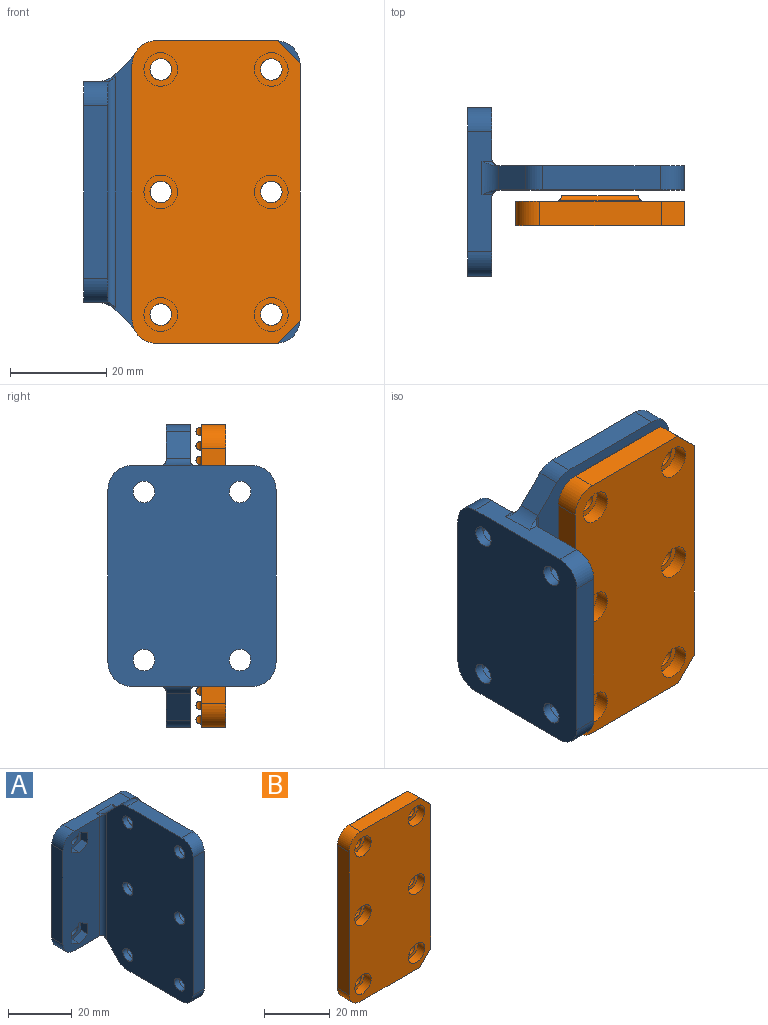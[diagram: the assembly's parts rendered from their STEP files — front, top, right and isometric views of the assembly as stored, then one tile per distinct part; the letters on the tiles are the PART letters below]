
ASSEMBLY  parts=2 mates=1
PART A: 118 faces, bbox 35x45x63 mm
  f0: cylinder r=2.25mm len=4.5mm, axis (-1,0,0), area 28.3mm2, adj f7,f87
  f1: cylinder r=2.25mm len=4.5mm, axis (-1,0,0), area 28.3mm2, adj f7,f80
  f2: cylinder r=2.25mm len=4.5mm, axis (-1,0,0), area 28.3mm2, adj f7,f73
  f3: cylinder r=2.25mm len=4.5mm, axis (-1,0,0), area 28.3mm2, adj f7,f66
  f4: cylinder r=2.25mm len=4.5mm, axis (-1,0,0), area 28.3mm2, adj f7,f59
  f5: cylinder r=2.25mm len=4.5mm, axis (-1,0,0), area 28.3mm2, adj f7,f52
  f6: plane 24.43x5mm, normal (0,0,1), area 122.1mm2, adj f7,f8,f95,f98
  f7: plane 63x39.07mm, normal (-1,0,0), area 2269.5mm2, adj f0,f1,f2,f3,f4,f5,f6,f20
  f8: plane 63x39.07mm, normal (1,0,0), area 2110.8mm2, adj f6,f20,f21,f50,f51,f53,f54,f55
  f9: cylinder r=2.25mm len=4.5mm, axis (0,1,0), area 28.3mm2, adj f19,f35
  f10: cylinder r=2.25mm len=4.5mm, axis (0,1,0), area 28.3mm2, adj f19,f28
  f11: cylinder r=2.25mm len=4.5mm, axis (0,1,0), area 28.3mm2, adj f19,f49
  f12: cylinder r=2.25mm len=4.5mm, axis (0,1,0), area 28.3mm2, adj f19,f42
  f13: plane 46x16.4mm, normal (0,-1,0), area 658.8mm2, adj f16,f17,f18,f22,f23,f24,f25,f26
  f14: plane 46x10.6mm, normal (0,-1,0), area 395.4mm2, adj f15,f16,f18,f36,f37,f38,f39,f41
  f15: plane 36x5mm, normal (1,0,0), area 180mm2, adj f14,f19,f100,f103
  f16: plane 25x5.09mm, normal (0,0,1), area 110.5mm2, adj f13,f14,f19,f97,f100,f101,f112,f113
  f17: plane 36x5mm, normal (-1,0,0), area 180mm2, adj f13,f19,f101,f102
  f18: plane 25x5.09mm, normal (0,0,-1), area 110.5mm2, adj f13,f14,f19,f96,f102,f103,f104,f113
  f19: plane 46x35mm, normal (0,1,0), area 1524.9mm2, adj f9,f10,f11,f12,f15,f16,f17,f18
  f20: plane 24.43x5mm, normal (0,0,-1), area 122.1mm2, adj f7,f8,f94,f99
  f21: plane 53x5mm, normal (0,-1,0), area 265mm2, adj f7,f8,f98,f99
  f22: plane 3.5x3mm, normal (0.5,0,0.87), area 12.1mm2, adj f13,f23,f27,f28
  f23: plane 3.5x3mm, normal (-0.5,0,0.87), area 12.1mm2, adj f13,f22,f24,f28
  f24: plane 4.04x3mm, normal (-1,0,0), area 12.1mm2, adj f13,f23,f25,f28
  f25: plane 3.5x3mm, normal (-0.5,0,-0.87), area 12.1mm2, adj f13,f24,f26,f28
  f26: plane 3.5x3mm, normal (0.5,0,-0.87), area 12.1mm2, adj f13,f25,f27,f28
  f27: plane 4.04x3mm, normal (1,0,0), area 12.1mm2, adj f13,f22,f26,f28
  f28: plane 8.08x7mm, normal (0,-1,0), area 26.5mm2, adj f10,f22,f23,f24,f25,f26,f27
  f29: plane 3.5x3mm, normal (0.5,0,0.87), area 12.1mm2, adj f13,f30,f34,f35
  f30: plane 3.5x3mm, normal (-0.5,0,0.87), area 12.1mm2, adj f13,f29,f31,f35
  f31: plane 4.04x3mm, normal (-1,0,0), area 12.1mm2, adj f13,f30,f32,f35
  f32: plane 3.5x3mm, normal (-0.5,0,-0.87), area 12.1mm2, adj f13,f31,f33,f35
  f33: plane 3.5x3mm, normal (0.5,0,-0.87), area 12.1mm2, adj f13,f32,f34,f35
  f34: plane 4.04x3mm, normal (1,0,0), area 12.1mm2, adj f13,f29,f33,f35
  f35: plane 8.08x7mm, normal (0,-1,0), area 26.5mm2, adj f9,f29,f30,f31,f32,f33,f34
  f36: plane 3.5x3mm, normal (-0.5,0,0.87), area 12.1mm2, adj f14,f37,f41,f42
  f37: plane 4.04x3mm, normal (-1,0,0), area 12.1mm2, adj f14,f36,f38,f42
  f38: plane 3.5x3mm, normal (-0.5,0,-0.87), area 12.1mm2, adj f14,f37,f39,f42
  f39: plane 3.51x3.01mm, normal (0.5,0,-0.87), area 12.1mm2, adj f14,f38,f40,f42,f107
  f40: plane 4.04x3mm, normal (1,0,0), area 12.1mm2, adj f39,f41,f42,f106
  f41: plane 3.5x3mm, normal (0.5,0,0.87), area 12.1mm2, adj f14,f36,f40,f42,f105
  f42: plane 8.08x7mm, normal (0,-1,0), area 26.5mm2, adj f12,f36,f37,f38,f39,f40,f41
  f43: plane 3.5x3mm, normal (-0.5,0,0.87), area 12.1mm2, adj f14,f44,f48,f49
  f44: plane 4.04x3mm, normal (-1,0,0), area 12.1mm2, adj f14,f43,f45,f49
  f45: plane 3.5x3mm, normal (-0.5,0,-0.87), area 12.1mm2, adj f14,f44,f46,f49
  f46: plane 3.51x3.01mm, normal (0.5,0,-0.87), area 12.1mm2, adj f14,f45,f47,f49,f111
  f47: plane 4.04x3mm, normal (1,0,0), area 12.1mm2, adj f46,f48,f49,f110
  f48: plane 3.5x3mm, normal (0.5,0,0.87), area 12.1mm2, adj f14,f43,f47,f49,f109
  f49: plane 8.08x7mm, normal (0,-1,0), area 26.5mm2, adj f11,f43,f44,f45,f46,f47,f48
  f50: plane 5.57x5.57mm, normal (0,0.71,0.71), area 39.4mm2, adj f7,f8,f95,f97
  f51: plane 5.57x5.57mm, normal (0,0.71,-0.71), area 39.4mm2, adj f7,f8,f94,f96
  f52: plane 8.08x7mm, normal (1,0,0), area 26.5mm2, adj f5,f53,f54,f55,f56,f57,f58
  f53: plane 3.5x3mm, normal (0,0.5,-0.87), area 12.1mm2, adj f8,f52,f54,f58
  f54: plane 4.04x3mm, normal (0,1,0), area 12.1mm2, adj f8,f52,f53,f55
  f55: plane 3.5x3mm, normal (0,0.5,0.87), area 12.1mm2, adj f8,f52,f54,f56
  f56: plane 3.5x3mm, normal (0,-0.5,0.87), area 12.1mm2, adj f8,f52,f55,f57
  f57: plane 4.04x3mm, normal (0,-1,0), area 12.1mm2, adj f8,f52,f56,f58
  f58: plane 3.5x3mm, normal (0,-0.5,-0.87), area 12.1mm2, adj f8,f52,f53,f57
  f59: plane 8.08x7mm, normal (1,0,0), area 26.5mm2, adj f4,f60,f61,f62,f63,f64,f65
  f60: plane 3.5x3mm, normal (0,0.5,-0.87), area 12.1mm2, adj f8,f59,f61,f65
  f61: plane 4.04x3mm, normal (0,1,0), area 12.1mm2, adj f8,f59,f60,f62
  f62: plane 3.5x3mm, normal (0,0.5,0.87), area 12.1mm2, adj f8,f59,f61,f63
  f63: plane 3.5x3mm, normal (0,-0.5,0.87), area 12.1mm2, adj f8,f59,f62,f64
  f64: plane 4.04x3mm, normal (0,-1,0), area 12.1mm2, adj f8,f59,f63,f65
  f65: plane 3.5x3mm, normal (0,-0.5,-0.87), area 12.1mm2, adj f8,f59,f60,f64
  f66: plane 8.08x7mm, normal (1,0,0), area 26.5mm2, adj f3,f67,f68,f69,f70,f71,f72
  f67: plane 3.5x3mm, normal (0,0.5,-0.87), area 12.1mm2, adj f8,f66,f68,f72
  f68: plane 4.04x3mm, normal (0,1,0), area 12.1mm2, adj f8,f66,f67,f69
  f69: plane 3.5x3mm, normal (0,0.5,0.87), area 12.1mm2, adj f8,f66,f68,f70
  f70: plane 3.5x3mm, normal (0,-0.5,0.87), area 12.1mm2, adj f8,f66,f69,f71
  f71: plane 4.04x3mm, normal (0,-1,0), area 12.1mm2, adj f8,f66,f70,f72
  f72: plane 3.5x3mm, normal (0,-0.5,-0.87), area 12.1mm2, adj f8,f66,f67,f71
  f73: plane 8.08x7mm, normal (1,0,0), area 26.5mm2, adj f2,f74,f75,f76,f77,f78,f79
  f74: plane 3.5x3mm, normal (0,-0.5,0.87), area 12.1mm2, adj f8,f73,f75,f79
  f75: plane 4.04x3mm, normal (0,-1,0), area 12.1mm2, adj f8,f73,f74,f76
  f76: plane 3.5x3mm, normal (0,-0.5,-0.87), area 12.1mm2, adj f8,f73,f75,f77
  f77: plane 3.5x3mm, normal (0,0.5,-0.87), area 12.1mm2, adj f8,f73,f76,f78
  f78: plane 4.04x3mm, normal (0,1,0), area 12.1mm2, adj f8,f73,f77,f79
  f79: plane 3.5x3mm, normal (0,0.5,0.87), area 12.1mm2, adj f8,f73,f74,f78
  f80: plane 8.08x7mm, normal (1,0,0), area 26.5mm2, adj f1,f81,f82,f83,f84,f85,f86
  f81: plane 3.5x3mm, normal (0,-0.5,0.87), area 12.1mm2, adj f8,f80,f82,f86
  f82: plane 4.04x3mm, normal (0,-1,0), area 12.1mm2, adj f8,f80,f81,f83
  f83: plane 3.5x3mm, normal (0,-0.5,-0.87), area 12.1mm2, adj f8,f80,f82,f84
  f84: plane 3.5x3mm, normal (0,0.5,-0.87), area 12.1mm2, adj f8,f80,f83,f85
  f85: plane 4.04x3mm, normal (0,1,0), area 12.1mm2, adj f8,f80,f84,f86
  f86: plane 3.5x3mm, normal (0,0.5,0.87), area 12.1mm2, adj f8,f80,f81,f85
  f87: plane 8.08x7mm, normal (1,0,0), area 26.5mm2, adj f0,f88,f89,f90,f91,f92,f93
  f88: plane 3.5x3mm, normal (0,-0.5,0.87), area 12.1mm2, adj f8,f87,f89,f93
  f89: plane 4.04x3mm, normal (0,-1,0), area 12.1mm2, adj f8,f87,f88,f90
  f90: plane 3.5x3mm, normal (0,-0.5,-0.87), area 12.1mm2, adj f8,f87,f89,f91
  f91: plane 3.5x3mm, normal (0,0.5,-0.87), area 12.1mm2, adj f8,f87,f90,f92
  f92: plane 4.04x3mm, normal (0,1,0), area 12.1mm2, adj f8,f87,f91,f93
  f93: plane 3.5x3mm, normal (0,0.5,0.87), area 12.1mm2, adj f8,f87,f88,f92
  f94: cylinder r=5mm len=5mm, axis (1,0,0), area 19.6mm2, adj f7,f8,f20,f51
  f95: cylinder r=5mm len=5mm, axis (1,0,0), area 19.6mm2, adj f6,f7,f8,f50
  f96: cylinder r=5mm len=7mm, axis (-1,0,0), area 22.9mm2, adj f7,f8,f18,f51,f116,f117
  f97: cylinder r=5mm len=7mm, axis (1,0,0), area 22.9mm2, adj f7,f8,f16,f50,f114,f115
  f98: cylinder r=5mm len=5mm, axis (1,0,0), area 39.3mm2, adj f6,f7,f8,f21
  f99: cylinder r=5mm len=5mm, axis (-1,0,0), area 39.3mm2, adj f7,f8,f20,f21
  f100: cylinder r=5mm len=5mm, axis (0,-1,0), area 39.3mm2, adj f14,f15,f16,f19
  f101: cylinder r=5mm len=5mm, axis (0,1,0), area 39.3mm2, adj f13,f16,f17,f19
  f102: cylinder r=5mm len=5mm, axis (0,-1,0), area 39.3mm2, adj f13,f17,f18,f19
  f103: cylinder r=5mm len=5mm, axis (0,1,0), area 39.3mm2, adj f14,f15,f18,f19
  f104: cylinder r=1.5mm len=4.25mm, axis (0,0,1), area 8.6mm2, adj f8,f14,f18,f105,f117
  f105: bspline ~1.54x1.54mm, area 0.8mm2, adj f8,f41,f104,f106
  f106: cylinder r=1.5mm len=4.04mm, axis (0,0,-1), area 7.4mm2, adj f8,f40,f105,f107
  f107: bspline ~1.54x1.53mm, area 0.8mm2, adj f8,f39,f106,f108
  f108: cylinder r=1.5mm len=30.5mm, axis (0,0,1), area 71.9mm2, adj f8,f14,f107,f109
  f109: bspline ~1.54x1.54mm, area 0.8mm2, adj f8,f48,f108,f110
  f110: cylinder r=1.5mm len=4.04mm, axis (0,0,-1), area 7.4mm2, adj f8,f47,f109,f111
  f111: bspline ~1.54x1.53mm, area 0.8mm2, adj f8,f46,f110,f112
  f112: cylinder r=1.5mm len=4.25mm, axis (0,0,1), area 8.6mm2, adj f8,f14,f16,f111,f115
  f113: cylinder r=1.5mm len=48mm, axis (0,0,-1), area 110.2mm2, adj f7,f13,f16,f18,f114,f116
  f114: cylinder r=1mm len=3.57mm, axis (0,-1,0), area 2.1mm2, adj f7,f16,f97,f113
  f115: cylinder r=1mm len=3.57mm, axis (0,-1,0), area 2.1mm2, adj f8,f16,f97,f112
  f116: cylinder r=1mm len=3.57mm, axis (0,-1,0), area 2.1mm2, adj f7,f18,f96,f113
  f117: cylinder r=1mm len=3.57mm, axis (0,-1,0), area 2.1mm2, adj f8,f18,f96,f104
PART B: 175 faces, bbox 35x6.2x63 mm
  f0: plane 63x35mm, normal (0,1,0), area 1206.4mm2, adj f1,f2,f3,f4,f5,f6,f7,f8
  f1: cylinder r=2.25mm len=4.5mm, axis (0,1,0), area 28.3mm2, adj f0,f17
  f2: cylinder r=2.25mm len=4.5mm, axis (0,1,0), area 28.3mm2, adj f0,f19
  f3: cylinder r=2.25mm len=4.5mm, axis (0,1,0), area 28.3mm2, adj f0,f21
  f4: cylinder r=2.25mm len=4.5mm, axis (0,1,0), area 28.3mm2, adj f0,f23
  f5: cylinder r=2.25mm len=4.5mm, axis (0,1,0), area 28.3mm2, adj f0,f13
  f6: cylinder r=2.25mm len=4.5mm, axis (0,1,0), area 28.3mm2, adj f0,f15
  f7: plane 53.4x5mm, normal (1,0,0), area 267mm2, adj f0,f11,f173,f174
  f8: plane 25.2x5mm, normal (0,0,1), area 126mm2, adj f0,f11,f171,f174
  f9: plane 53x5mm, normal (-1,0,0), area 265mm2, adj f0,f11,f171,f172
  f10: plane 25.2x5mm, normal (0,0,-1), area 126mm2, adj f0,f11,f172,f173
  f11: plane 63x35mm, normal (0,-1,0), area 1940.3mm2, adj f7,f8,f9,f10,f12,f14,f16,f18
  f12: cylinder r=3.5mm len=7mm, axis (0,-1,0), area 66mm2, adj f11,f13
  f13: plane 7x7mm, normal (0,-1,0), area 22.6mm2, adj f5,f12
  f14: cylinder r=3.5mm len=7mm, axis (0,-1,0), area 66mm2, adj f11,f15
  f15: plane 7x7mm, normal (0,-1,0), area 22.6mm2, adj f6,f14
  f16: cylinder r=3.5mm len=7mm, axis (0,-1,0), area 66mm2, adj f11,f17
  f17: plane 7x7mm, normal (0,-1,0), area 22.6mm2, adj f1,f16
  f18: cylinder r=3.5mm len=7mm, axis (0,-1,0), area 66mm2, adj f11,f19
  f19: plane 7x7mm, normal (0,-1,0), area 22.6mm2, adj f2,f18
  f20: cylinder r=3.5mm len=7mm, axis (0,-1,0), area 66mm2, adj f11,f21
  f21: plane 7x7mm, normal (0,-1,0), area 22.6mm2, adj f3,f20
  f22: cylinder r=3.5mm len=7mm, axis (0,-1,0), area 66mm2, adj f11,f23
  f23: plane 7x7mm, normal (0,-1,0), area 22.6mm2, adj f4,f22
  f24: cylinder r=0.26mm len=18.33mm, axis (-1,0,0), area 7.3mm2, adj f0,f25,f169,f170
  f25: cylinder r=0.87mm len=16.84mm, axis (-1,0,0), area 45.2mm2, adj f24,f26,f27,f28,f169,f170
  f26: cylinder r=0.26mm len=18.33mm, axis (-1,0,0), area 7.3mm2, adj f0,f25,f169,f170
  f27: plane 0.19x0.01mm, normal (1,0,0), area 0mm2, adj f25,f170
  f28: plane 0.19x0.01mm, normal (-1,0,0), area 0mm2, adj f25,f169
  f29: cylinder r=0.26mm len=18.33mm, axis (-1,0,0), area 7.3mm2, adj f0,f31,f167,f168
  f30: cylinder r=0.26mm len=18.33mm, axis (-1,0,0), area 7.3mm2, adj f0,f31,f167,f168
  f31: cylinder r=0.87mm len=16.84mm, axis (-1,0,0), area 45.2mm2, adj f29,f30,f32,f33,f167,f168
  f32: plane 0.19x0.01mm, normal (1,0,0), area 0mm2, adj f31,f168
  f33: plane 0.19x0.01mm, normal (-1,0,0), area 0mm2, adj f31,f167
  f34: cylinder r=0.26mm len=18.33mm, axis (-1,0,0), area 7.3mm2, adj f0,f36,f165,f166
  f35: cylinder r=0.26mm len=18.33mm, axis (-1,0,0), area 7.3mm2, adj f0,f36,f165,f166
  f36: cylinder r=0.87mm len=16.84mm, axis (-1,0,0), area 45.2mm2, adj f34,f35,f37,f38,f165,f166
  f37: plane 0.19x0.01mm, normal (1,0,0), area 0mm2, adj f36,f166
  f38: plane 0.19x0.01mm, normal (-1,0,0), area 0mm2, adj f36,f165
  f39: cylinder r=0.26mm len=18.33mm, axis (-1,0,0), area 7.3mm2, adj f0,f40,f163,f164
  f40: cylinder r=0.87mm len=16.84mm, axis (-1,0,0), area 45.2mm2, adj f39,f41,f42,f43,f163,f164
  f41: cylinder r=0.26mm len=18.33mm, axis (-1,0,0), area 7.3mm2, adj f0,f40,f163,f164
  f42: plane 0.19x0.01mm, normal (1,0,0), area 0mm2, adj f40,f164
  f43: plane 0.19x0.01mm, normal (-1,0,0), area 0mm2, adj f40,f163
  f44: cylinder r=0.26mm len=18.33mm, axis (-1,0,0), area 7.3mm2, adj f0,f46,f161,f162
  f45: cylinder r=0.26mm len=18.33mm, axis (-1,0,0), area 7.3mm2, adj f0,f46,f161,f162
  f46: cylinder r=0.87mm len=16.84mm, axis (-1,0,0), area 45.2mm2, adj f44,f45,f47,f48,f161,f162
  f47: plane 0.19x0.01mm, normal (1,0,0), area 0mm2, adj f46,f162
  f48: plane 0.19x0.01mm, normal (-1,0,0), area 0mm2, adj f46,f161
  f49: cylinder r=0.26mm len=18.33mm, axis (-1,0,0), area 7.3mm2, adj f0,f50,f159,f160
  f50: cylinder r=0.87mm len=16.84mm, axis (-1,0,0), area 45.2mm2, adj f49,f51,f52,f53,f159,f160
  f51: cylinder r=0.26mm len=18.33mm, axis (-1,0,0), area 7.3mm2, adj f0,f50,f159,f160
  f52: plane 0.19x0.01mm, normal (1,0,0), area 0mm2, adj f50,f160
  f53: plane 0.19x0.01mm, normal (-1,0,0), area 0mm2, adj f50,f159
  f54: cylinder r=0.26mm len=18.33mm, axis (-1,0,0), area 7.3mm2, adj f0,f56,f157,f158
  f55: cylinder r=0.26mm len=18.33mm, axis (-1,0,0), area 7.3mm2, adj f0,f56,f157,f158
  f56: cylinder r=0.87mm len=16.84mm, axis (-1,0,0), area 45.2mm2, adj f54,f55,f57,f58,f157,f158
  f57: plane 0.19x0.01mm, normal (1,0,0), area 0mm2, adj f56,f158
  f58: plane 0.19x0.01mm, normal (-1,0,0), area 0mm2, adj f56,f157
  f59: cylinder r=0.26mm len=18.33mm, axis (-1,0,0), area 7.3mm2, adj f0,f60,f155,f156
  f60: cylinder r=0.87mm len=16.84mm, axis (-1,0,0), area 45.2mm2, adj f59,f61,f62,f63,f155,f156
  f61: cylinder r=0.26mm len=18.33mm, axis (-1,0,0), area 7.3mm2, adj f0,f60,f155,f156
  f62: plane 0.19x0.01mm, normal (1,0,0), area 0mm2, adj f60,f156
  f63: plane 0.19x0.01mm, normal (-1,0,0), area 0mm2, adj f60,f155
  f64: cylinder r=0.26mm len=18.33mm, axis (-1,0,0), area 7.3mm2, adj f0,f66,f153,f154
  f65: cylinder r=0.26mm len=18.33mm, axis (-1,0,0), area 7.3mm2, adj f0,f66,f153,f154
  f66: cylinder r=0.87mm len=16.84mm, axis (-1,0,0), area 45.2mm2, adj f64,f65,f67,f68,f153,f154
  f67: plane 0.19x0.01mm, normal (1,0,0), area 0mm2, adj f66,f154
  f68: plane 0.19x0.01mm, normal (-1,0,0), area 0mm2, adj f66,f153
  f69: cylinder r=0.26mm len=18.33mm, axis (-1,0,0), area 7.3mm2, adj f0,f70,f151,f152
  f70: cylinder r=0.87mm len=16.84mm, axis (-1,0,0), area 45.2mm2, adj f69,f71,f72,f73,f151,f152
  f71: cylinder r=0.26mm len=18.33mm, axis (-1,0,0), area 7.3mm2, adj f0,f70,f151,f152
  f72: plane 0.19x0.01mm, normal (1,0,0), area 0mm2, adj f70,f152
  f73: plane 0.19x0.01mm, normal (-1,0,0), area 0mm2, adj f70,f151
  f74: cylinder r=0.26mm len=18.33mm, axis (-1,0,0), area 7.3mm2, adj f0,f76,f149,f150
  f75: cylinder r=0.26mm len=18.33mm, axis (-1,0,0), area 7.3mm2, adj f0,f76,f149,f150
  f76: cylinder r=0.87mm len=16.84mm, axis (-1,0,0), area 45.2mm2, adj f74,f75,f77,f78,f149,f150
  f77: plane 0.19x0.01mm, normal (1,0,0), area 0mm2, adj f76,f150
  f78: plane 0.19x0.01mm, normal (-1,0,0), area 0mm2, adj f76,f149
  f79: cylinder r=0.26mm len=18.33mm, axis (-1,0,0), area 7.3mm2, adj f0,f80,f147,f148
  f80: cylinder r=0.87mm len=16.84mm, axis (-1,0,0), area 45.2mm2, adj f79,f81,f82,f83,f147,f148
  f81: cylinder r=0.26mm len=18.33mm, axis (-1,0,0), area 7.3mm2, adj f0,f80,f147,f148
  f82: plane 0.19x0.01mm, normal (1,0,0), area 0mm2, adj f80,f148
  f83: plane 0.19x0.01mm, normal (-1,0,0), area 0mm2, adj f80,f147
  f84: cylinder r=0.26mm len=18.33mm, axis (-1,0,0), area 7.3mm2, adj f0,f86,f145,f146
  f85: cylinder r=0.26mm len=18.33mm, axis (-1,0,0), area 7.3mm2, adj f0,f86,f145,f146
  f86: cylinder r=0.87mm len=16.84mm, axis (-1,0,0), area 45.2mm2, adj f84,f85,f87,f88,f145,f146
  f87: plane 0.19x0.01mm, normal (1,0,0), area 0mm2, adj f86,f146
  f88: plane 0.19x0.01mm, normal (-1,0,0), area 0mm2, adj f86,f145
  f89: cylinder r=0.26mm len=18.33mm, axis (-1,0,0), area 7.3mm2, adj f0,f90,f143,f144
  f90: cylinder r=0.87mm len=16.84mm, axis (-1,0,0), area 45.2mm2, adj f89,f91,f92,f93,f143,f144
  f91: cylinder r=0.26mm len=18.33mm, axis (-1,0,0), area 7.3mm2, adj f0,f90,f143,f144
  f92: plane 0.19x0.01mm, normal (1,0,0), area 0mm2, adj f90,f144
  f93: plane 0.19x0.01mm, normal (-1,0,0), area 0mm2, adj f90,f143
  f94: cylinder r=0.26mm len=18.33mm, axis (-1,0,0), area 7.3mm2, adj f0,f96,f141,f142
  f95: cylinder r=0.26mm len=18.33mm, axis (-1,0,0), area 7.3mm2, adj f0,f96,f141,f142
  f96: cylinder r=0.87mm len=16.84mm, axis (-1,0,0), area 45.2mm2, adj f94,f95,f97,f98,f141,f142
  f97: plane 0.19x0.01mm, normal (1,0,0), area 0mm2, adj f96,f142
  f98: plane 0.19x0.01mm, normal (-1,0,0), area 0mm2, adj f96,f141
  f99: cylinder r=0.26mm len=18.33mm, axis (-1,0,0), area 7.3mm2, adj f0,f100,f139,f140
  f100: cylinder r=0.87mm len=16.84mm, axis (-1,0,0), area 45.2mm2, adj f99,f101,f102,f103,f139,f140
  f101: cylinder r=0.26mm len=18.33mm, axis (-1,0,0), area 7.3mm2, adj f0,f100,f139,f140
  f102: plane 0.19x0.01mm, normal (1,0,0), area 0mm2, adj f100,f140
  f103: plane 0.19x0.01mm, normal (-1,0,0), area 0mm2, adj f100,f139
  f104: cylinder r=0.26mm len=18.33mm, axis (-1,0,0), area 7.3mm2, adj f0,f106,f137,f138
  f105: cylinder r=0.26mm len=18.33mm, axis (-1,0,0), area 7.3mm2, adj f0,f106,f137,f138
  f106: cylinder r=0.87mm len=16.84mm, axis (-1,0,0), area 45.2mm2, adj f104,f105,f107,f108,f137,f138
  f107: plane 0.19x0.01mm, normal (1,0,0), area 0mm2, adj f106,f138
  f108: plane 0.19x0.01mm, normal (-1,0,0), area 0mm2, adj f106,f137
  f109: cylinder r=0.26mm len=18.33mm, axis (-1,0,0), area 7.3mm2, adj f0,f110,f135,f136
  f110: cylinder r=0.87mm len=16.84mm, axis (-1,0,0), area 45.2mm2, adj f109,f111,f112,f113,f135,f136
  f111: cylinder r=0.26mm len=18.33mm, axis (-1,0,0), area 7.3mm2, adj f0,f110,f135,f136
  f112: plane 0.19x0.01mm, normal (1,0,0), area 0mm2, adj f110,f136
  f113: plane 0.19x0.01mm, normal (-1,0,0), area 0mm2, adj f110,f135
  f114: cylinder r=0.26mm len=18.33mm, axis (-1,0,0), area 7.3mm2, adj f0,f116,f133,f134
  f115: cylinder r=0.26mm len=18.33mm, axis (-1,0,0), area 7.3mm2, adj f0,f116,f133,f134
  f116: cylinder r=0.87mm len=16.84mm, axis (-1,0,0), area 45.2mm2, adj f114,f115,f117,f118,f133,f134
  f117: plane 0.19x0.01mm, normal (1,0,0), area 0mm2, adj f116,f134
  f118: plane 0.19x0.01mm, normal (-1,0,0), area 0mm2, adj f116,f133
  f119: cylinder r=0.26mm len=18.33mm, axis (-1,0,0), area 7.3mm2, adj f0,f120,f131,f132
  f120: cylinder r=0.87mm len=16.84mm, axis (-1,0,0), area 45.2mm2, adj f119,f121,f122,f123,f131,f132
  f121: cylinder r=0.26mm len=18.33mm, axis (-1,0,0), area 7.3mm2, adj f0,f120,f131,f132
  f122: plane 0.19x0.01mm, normal (1,0,0), area 0mm2, adj f120,f132
  f123: plane 0.19x0.01mm, normal (-1,0,0), area 0mm2, adj f120,f131
  f124: cylinder r=0.26mm len=18.33mm, axis (-1,0,0), area 7.3mm2, adj f0,f125,f129,f130
  f125: cylinder r=0.87mm len=16.84mm, axis (-1,0,0), area 45.2mm2, adj f124,f126,f127,f128,f129,f130
  f126: cylinder r=0.26mm len=18.33mm, axis (-1,0,0), area 7.3mm2, adj f0,f125,f129,f130
  f127: plane 0.19x0.01mm, normal (1,0,0), area 0mm2, adj f125,f130
  f128: plane 0.19x0.01mm, normal (-1,0,0), area 0mm2, adj f125,f129
  f129: cylinder r=1.17mm len=2.26mm, axis (0,0,1), area 3mm2, adj f0,f124,f125,f126,f128
  f130: cylinder r=1.17mm len=2.26mm, axis (0,0,-1), area 3mm2, adj f0,f124,f125,f126,f127
  f131: cylinder r=1.17mm len=2.26mm, axis (0,0,1), area 3mm2, adj f0,f119,f120,f121,f123
  f132: cylinder r=1.17mm len=2.26mm, axis (0,0,-1), area 3mm2, adj f0,f119,f120,f121,f122
  f133: cylinder r=1.17mm len=2.26mm, axis (0,0,1), area 3mm2, adj f0,f114,f115,f116,f118
  f134: cylinder r=1.17mm len=2.26mm, axis (0,0,-1), area 3mm2, adj f0,f114,f115,f116,f117
  f135: cylinder r=1.17mm len=2.26mm, axis (0,0,1), area 3mm2, adj f0,f109,f110,f111,f113
  f136: cylinder r=1.17mm len=2.26mm, axis (0,0,-1), area 3mm2, adj f0,f109,f110,f111,f112
  f137: cylinder r=1.17mm len=2.26mm, axis (0,0,1), area 3mm2, adj f0,f104,f105,f106,f108
  f138: cylinder r=1.17mm len=2.26mm, axis (0,0,-1), area 3mm2, adj f0,f104,f105,f106,f107
  f139: cylinder r=1.17mm len=2.26mm, axis (0,0,1), area 3mm2, adj f0,f99,f100,f101,f103
  f140: cylinder r=1.17mm len=2.26mm, axis (0,0,-1), area 3mm2, adj f0,f99,f100,f101,f102
  f141: cylinder r=1.17mm len=2.26mm, axis (0,0,1), area 3mm2, adj f0,f94,f95,f96,f98
  f142: cylinder r=1.17mm len=2.26mm, axis (0,0,-1), area 3mm2, adj f0,f94,f95,f96,f97
  f143: cylinder r=1.17mm len=2.26mm, axis (0,0,1), area 3mm2, adj f0,f89,f90,f91,f93
  f144: cylinder r=1.17mm len=2.26mm, axis (0,0,-1), area 3mm2, adj f0,f89,f90,f91,f92
  f145: cylinder r=1.17mm len=2.26mm, axis (0,0,1), area 3mm2, adj f0,f84,f85,f86,f88
  f146: cylinder r=1.17mm len=2.26mm, axis (0,0,-1), area 3mm2, adj f0,f84,f85,f86,f87
  f147: cylinder r=1.17mm len=2.26mm, axis (0,0,1), area 3mm2, adj f0,f79,f80,f81,f83
  f148: cylinder r=1.17mm len=2.26mm, axis (0,0,-1), area 3mm2, adj f0,f79,f80,f81,f82
  f149: cylinder r=1.17mm len=2.26mm, axis (0,0,1), area 3mm2, adj f0,f74,f75,f76,f78
  f150: cylinder r=1.17mm len=2.26mm, axis (0,0,-1), area 3mm2, adj f0,f74,f75,f76,f77
  f151: cylinder r=1.17mm len=2.26mm, axis (0,0,1), area 3mm2, adj f0,f69,f70,f71,f73
  f152: cylinder r=1.17mm len=2.26mm, axis (0,0,-1), area 3mm2, adj f0,f69,f70,f71,f72
  f153: cylinder r=1.17mm len=2.26mm, axis (0,0,1), area 3mm2, adj f0,f64,f65,f66,f68
  f154: cylinder r=1.17mm len=2.26mm, axis (0,0,-1), area 3mm2, adj f0,f64,f65,f66,f67
  f155: cylinder r=1.17mm len=2.26mm, axis (0,0,1), area 3mm2, adj f0,f59,f60,f61,f63
  f156: cylinder r=1.17mm len=2.26mm, axis (0,0,-1), area 3mm2, adj f0,f59,f60,f61,f62
  f157: cylinder r=1.17mm len=2.26mm, axis (0,0,1), area 3mm2, adj f0,f54,f55,f56,f58
  f158: cylinder r=1.17mm len=2.26mm, axis (0,0,-1), area 3mm2, adj f0,f54,f55,f56,f57
  f159: cylinder r=1.17mm len=2.26mm, axis (0,0,1), area 3mm2, adj f0,f49,f50,f51,f53
  f160: cylinder r=1.17mm len=2.26mm, axis (0,0,-1), area 3mm2, adj f0,f49,f50,f51,f52
  f161: cylinder r=1.17mm len=2.26mm, axis (0,0,1), area 3mm2, adj f0,f44,f45,f46,f48
  f162: cylinder r=1.17mm len=2.26mm, axis (0,0,-1), area 3mm2, adj f0,f44,f45,f46,f47
  f163: cylinder r=1.17mm len=2.26mm, axis (0,0,1), area 3mm2, adj f0,f39,f40,f41,f43
  f164: cylinder r=1.17mm len=2.26mm, axis (0,0,-1), area 3mm2, adj f0,f39,f40,f41,f42
  f165: cylinder r=1.17mm len=2.26mm, axis (0,0,1), area 3mm2, adj f0,f34,f35,f36,f38
  f166: cylinder r=1.17mm len=2.26mm, axis (0,0,-1), area 3mm2, adj f0,f34,f35,f36,f37
  f167: cylinder r=1.17mm len=2.26mm, axis (0,0,1), area 3mm2, adj f0,f29,f30,f31,f33
  f168: cylinder r=1.17mm len=2.26mm, axis (0,0,-1), area 3mm2, adj f0,f29,f30,f31,f32
  f169: cylinder r=1.17mm len=2.26mm, axis (0,0,1), area 3mm2, adj f0,f24,f25,f26,f28
  f170: cylinder r=1.17mm len=2.26mm, axis (0,0,-1), area 3mm2, adj f0,f24,f25,f26,f27
  f171: cylinder r=5mm len=5mm, axis (0,1,0), area 39.3mm2, adj f0,f8,f9,f11
  f172: cylinder r=5mm len=5mm, axis (0,-1,0), area 39.3mm2, adj f0,f9,f10,f11
  f173: plane 5x4.8mm, normal (0.71,0,-0.71), area 33.9mm2, adj f0,f7,f10,f11
  f174: plane 5x4.8mm, normal (0.71,0,0.71), area 33.9mm2, adj f0,f7,f8,f11
PLACE A rot(axis=(0,0,1),90deg) t=(2.5,0,0)mm
PLACE B t=(27.5,-4.5,0)mm
MATE fastened B.f2 <-> A.f3  axis (0,1,0) through (39,-2,25.5)mm
